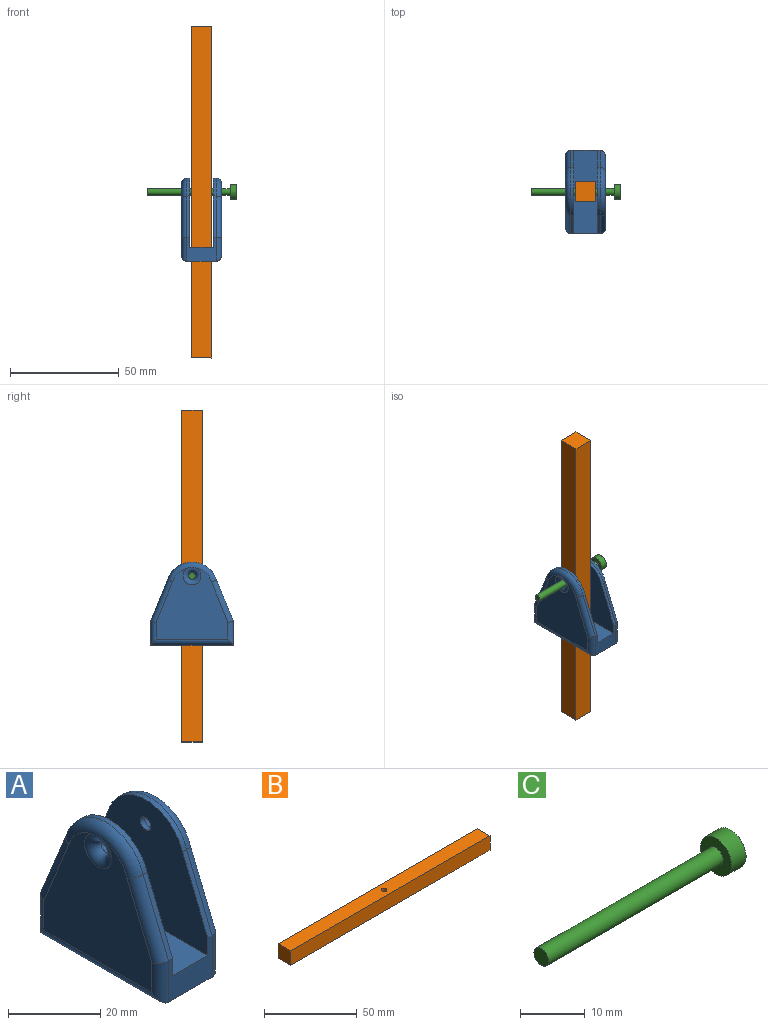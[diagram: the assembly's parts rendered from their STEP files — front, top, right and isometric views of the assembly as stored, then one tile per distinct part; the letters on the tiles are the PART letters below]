
ASSEMBLY  parts=3 mates=4
PART A: 32 faces, bbox 18.4x38.1x39.1 mm
  f0: plane 38.1x13.34mm, normal (0,0,-1), area 508.1mm2, adj f4,f5,f9,f31
  f1: plane 18.97x7.78mm, normal (0,-0.93,0.38), area 26mm2, adj f2,f5,f8,f12
  f2: cylinder r=11.86mm len=22.55mm, axis (1,0,0), area 37.8mm2, adj f1,f3,f8,f14
  f3: plane 18.97x7.78mm, normal (0,0.93,0.38), area 26mm2, adj f2,f4,f8,f13
  f4: plane 13.34x10.96mm, normal (0,1,0), area 96.4mm2, adj f0,f3,f8,f11,f16,f17,f19,f28
  f5: plane 13.34x10.96mm, normal (0,-1,0), area 96.4mm2, adj f0,f1,f8,f10,f16,f18,f21,f28
  f6: plane 33.02x32.79mm, normal (1,0,0), area 765.9mm2, adj f9,f10,f11,f12,f13,f14,f15
  f7: cylinder r=1.59mm len=3.18mm, axis (1,0,0), area 12.7mm2, adj f8,f15
  f8: plane 38.1x31.75mm, normal (-1,0,0), area 877.8mm2, adj f1,f2,f3,f4,f5,f7,f28
  f9: cylinder r=2.54mm len=38.1mm, axis (0,1,0), area 144.6mm2, adj f0,f6,f10,f11
  f10: cylinder r=2.54mm len=10.96mm, axis (0,0,-1), area 39.3mm2, adj f5,f6,f9,f12
  f11: cylinder r=2.54mm len=10.96mm, axis (0,0,1), area 39.3mm2, adj f4,f6,f9,f13
  f12: cylinder r=2.54mm len=20.02mm, axis (0,-0.38,-0.93), area 81.3mm2, adj f1,f6,f10,f14
  f13: cylinder r=2.54mm len=20.02mm, axis (0,-0.38,0.93), area 81.3mm2, adj f3,f6,f11,f14
  f14: torus R=9.32mm, axis (1,0,0), area 109.5mm2, adj f2,f6,f12,f13,f15
  f15: torus R=4.13mm, axis (1,0,0), area 62.5mm2, adj f6,f7,f14
  f16: plane 38.1x31.75mm, normal (1,0,0), area 877.8mm2, adj f4,f5,f19,f20,f21,f22,f28,f30
  f17: cylinder r=2.54mm len=10.96mm, axis (0,0,-1), area 39.3mm2, adj f4,f23,f24,f31
  f18: cylinder r=2.54mm len=10.96mm, axis (0,0,1), area 39.3mm2, adj f5,f23,f25,f31
  f19: plane 18.89x7.74mm, normal (0,0.93,0.38), area 25.9mm2, adj f4,f16,f24,f30
  f20: cylinder r=11.86mm len=22.52mm, axis (1,0,0), area 37.7mm2, adj f16,f21,f26,f30
  f21: plane 18.97x7.78mm, normal (0,-0.93,0.38), area 26mm2, adj f5,f16,f20,f25
  f22: cylinder r=1.59mm len=3.18mm, axis (1,0,0), area 12.7mm2, adj f16,f27
  f23: plane 33.02x32.79mm, normal (-1,0,0), area 765.9mm2, adj f17,f18,f24,f25,f26,f27,f31
  f24: cylinder r=2.54mm len=20.02mm, axis (0,0.38,-0.93), area 81.1mm2, adj f17,f19,f23,f29
  f25: cylinder r=2.54mm len=20.02mm, axis (0,0.38,0.93), area 81.3mm2, adj f18,f21,f23,f26
  f26: torus R=9.32mm, axis (1,0,0), area 109.2mm2, adj f20,f23,f25,f27,f29
  f27: torus R=4.13mm, axis (1,0,0), area 62.5mm2, adj f22,f23,f26
  f28: plane 38.1x10.8mm, normal (0,0,1), area 411.3mm2, adj f4,f5,f8,f16
  f29: bspline ~3.11x2.42mm, area 0.4mm2, adj f24,f26,f30
  f30: cylinder r=2.54mm len=1.27mm, axis (1,0,0), area 0.2mm2, adj f16,f19,f20,f29
  f31: cylinder r=2.54mm len=38.1mm, axis (0,-1,0), area 144.6mm2, adj f0,f17,f18,f23
PART B: 7 faces, bbox 152.4x9.5x9.5 mm
  f0: plane 152.4x9.53mm, normal (0,-1,0), area 1451.6mm2, adj f1,f3,f4,f5
  f1: plane 9.53x9.53mm, normal (1,0,0), area 90.7mm2, adj f0,f2,f4,f5
  f2: plane 152.4x9.53mm, normal (0,1,0), area 1451.6mm2, adj f1,f3,f4,f5
  f3: plane 9.53x9.53mm, normal (-1,0,0), area 90.7mm2, adj f0,f2,f4,f5
  f4: plane 152.4x9.53mm, normal (0,0,1), area 1443.7mm2, adj f0,f1,f2,f3,f6
  f5: plane 152.4x9.53mm, normal (0,0,-1), area 1443.7mm2, adj f0,f1,f2,f3,f6
  f6: cylinder r=1.59mm len=9.53mm, axis (0,0,1), area 95mm2, adj f4,f5
PART C: 5 faces, bbox 41.3x6.8x6.8 mm
  f0: cylinder r=1.59mm len=38.1mm, axis (-1,0,0), area 380mm2, adj f1,f4
  f1: plane 3.18x3.18mm, normal (-1,0,0), area 7.9mm2, adj f0
  f2: cylinder r=3.4mm len=6.79mm, axis (-1,0,0), area 67.7mm2, adj f3,f4
  f3: plane 6.79x6.79mm, normal (1,0,0), area 36.2mm2, adj f2
  f4: plane 6.79x6.79mm, normal (-1,0,0), area 28.3mm2, adj f0,f2
PLACE A rot(axis=(-1,0.04,0.04),0deg) t=(-11.19,40.91,-2.93)mm
PLACE B rot(axis=(0,-1,0),90deg) t=(-15.63,5.82,105.02)mm
PLACE C rot(axis=(-1,0.02,0.03),0deg) t=(-45.39,15.25,17.35)mm
MATE cylindrical C.f0 <-> A.f27  axis (-1,0,0) through (-26.34,1.06,28.82)mm
MATE parallel B.f6 <-> A.f27  axis (-1,0,0) through (-25.16,1.06,28.82)mm
MATE slider A.f27 <-> A.f27  axis (1,0,0) through (-13.73,1.06,28.82)mm
MATE revolute A.f27 <-> B.f6  axis (-1,0,0) through (-15,1.06,28.82)mm
